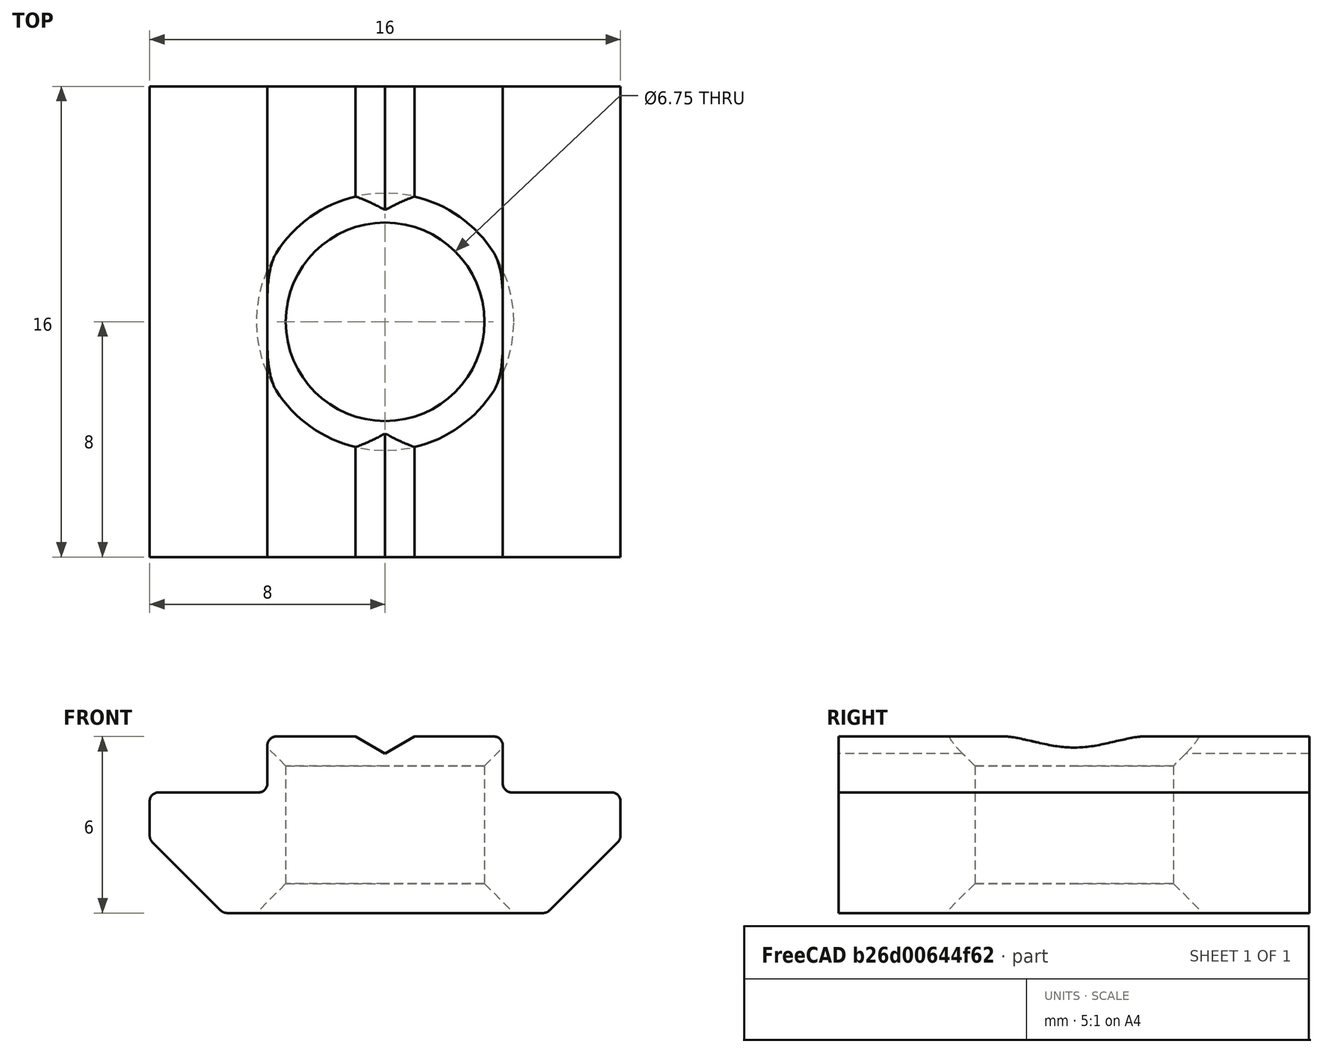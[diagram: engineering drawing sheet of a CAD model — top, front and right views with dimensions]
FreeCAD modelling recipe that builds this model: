
FCSTD DOCUMENT  (FreeCAD 0.19R20514 (Git))
Label: AP3030S8_StoneM8Heavy
Comment: FreeCAD-Library by episource -- https://github.com/episource/FreeCAD-Library
License: Creative Commons Attribution
LicenseURL: http://creativecommons.org/licenses/by/4.0/
objects: TechDraw::DrawViewDimension×10, Sketcher::SketchObject×3, TechDraw::DrawViewPart×2, TechDraw::DrawViewClip×2, TechDraw::DrawSVGTemplate×1, PartDesign::CoordinateSystem×1, App::DocumentObjectGroup×1, PartDesign::Pad×1, PartDesign::Hole×1, PartDesign::Groove×1, PartDesign::Body×1, TechDraw::DrawPage×1, App::Part×1
note: 11 computed .brp shape members not serialized (recipe doc carries the construction recipe); baked Part::Feature solids carry a one-line shape summary decoded from their .brp

FEATURE [Sketcher::SketchObject] Sketch001  label="PocketM6"
  Placement = pos=(0,0,6) rot=(0,0,1;0rad)
  sketch-geometry (1):
    g0: Circle CenterX=0 CenterY=0 CenterZ=0 NormalX=0 NormalY=0 NormalZ=1 AngleXU=0 Radius=0.715801
  constraints (1):
    c: Coincident(g0,g-1)
FEATURE [TechDraw::DrawSVGTemplate] Template
  EditableTexts = FC-SC=Scale 2:1 [mm]
  Height = 210
  Orientation = 1
  Width = 297
FEATURE [PartDesign::CoordinateSystem] AssyMount
  AttacherType = Attacher::AttachEngine3D
  AttachmentOffset = pos=(0,0,6.3) rot=(0,0,1;0rad)
  MapMode = 5
  Placement = pos=(0,0,6.3) rot=(0,0,1;0rad)
  Support = -> [XY_Plane]
  expr: .AttachmentOffset.Base.z = <<Variables>>.StoneHeight + <<Variables>>.ProfileSlotRise - <<Variables>>.StoneRise
FEATURE [App::DocumentObjectGroup] Group  label="Variables"
  ProfileSlotRise = 2.2
  ScrewHoleBevelSize = 1
  SlotWidth = 8
  StoneFillet = 0.3
  StoneHeight = 6
  StoneLength = 16
  StoneOuterRise = 1.6
  StoneTopNotchDepth = 0.58
  StoneTopNotchWidth = 2
  StoneTopRise = 1.9
  StoneWidth = 16
FEATURE [Sketcher::SketchObject] Sketch  label="StoneSectionSketch"
  MapMode = 5
  Placement = pos=(0,0,0) rot=(1,0,0;1.5708rad)
  Support = -> [XZ_Plane]
  expr: Constraints[16] = <<Variables>>.StoneFillet
  expr: Constraints[19] = <<Variables>>.StoneFillet
  expr: Constraints[23] = <<Variables>>.StoneFillet
  expr: Constraints[18] = <<Variables>>.StoneFillet
  expr: Constraints[15] = <<Variables>>.StoneFillet
  expr: Constraints[20] = <<Variables>>.StoneFillet
  expr: Constraints[24] = <<Variables>>.StoneFillet
  expr: Constraints[14] = <<Variables>>.StoneTopRise
  expr: Constraints[22] = <<Variables>>.StoneFillet
  expr: Constraints[27] = <<Variables>>.StoneTopNotchWidth
  expr: Constraints[17] = <<Variables>>.StoneFillet
  expr: Constraints[25] = <<Variables>>.StoneTopNotchDepth
  expr: Constraints[21] = <<Variables>>.StoneFillet
  expr: Constraints[13] = <<Variables>>.StoneHeight
  expr: Constraints[12] = <<Variables>>.StoneWidth
  expr: Constraints[11] = <<Variables>>.SlotWidth
  expr: Constraints[64] = <<Variables>>.StoneOuterRise
  sketch-geometry (26):
    g0: LineSegment StartX=-1 StartY=6 StartZ=0 EndX=-3.7 EndY=6 EndZ=0
    g1: ArcOfCircle CenterX=-3.7 CenterY=5.7 CenterZ=0 NormalX=0 NormalY=0 NormalZ=1 AngleXU=3.14159 Radius=0.3 StartAngle=4.71239 EndAngle=6.28319
    g2: LineSegment StartX=-4 StartY=5.7 StartZ=0 EndX=-4 EndY=4.4 EndZ=0
    g3: ArcOfCircle CenterX=-4.3 CenterY=4.4 CenterZ=0 NormalX=0 NormalY=0 NormalZ=1 AngleXU=-3.14159 Radius=0.3 StartAngle=1.5708 EndAngle=3.14159
    g4: LineSegment StartX=-4.3 StartY=4.1 StartZ=0 EndX=-7.7 EndY=4.1 EndZ=0
    g5: ArcOfCircle CenterX=-7.7 CenterY=3.8 CenterZ=0 NormalX=0 NormalY=0 NormalZ=1 AngleXU=-3.14159 Radius=0.3 StartAngle=4.71239 EndAngle=6.28319
    g6: LineSegment StartX=-8 StartY=3.8 StartZ=0 EndX=-8 EndY=2.62426 EndZ=0
    g7: ArcOfCircle CenterX=-7.7 CenterY=2.62426 CenterZ=0 NormalX=0 NormalY=0 NormalZ=1 AngleXU=-3.14159 Radius=0.3 StartAngle=0 EndAngle=0.785398
    g8: LineSegment StartX=-7.91213 StartY=2.41213 StartZ=0 EndX=-5.58787 EndY=0.087868 EndZ=0
    g9: ArcOfCircle CenterX=-5.37574 CenterY=0.3 CenterZ=0 NormalX=0 NormalY=0 NormalZ=1 AngleXU=3.14159 Radius=0.3 StartAngle=0.785398 EndAngle=1.5708
    g10: LineSegment StartX=-5.37574 StartY=0 StartZ=0 EndX=5.37574 EndY=0 EndZ=0
    g11: ArcOfCircle CenterX=5.37574 CenterY=0.3 CenterZ=0 NormalX=0 NormalY=0 NormalZ=1 AngleXU=-3.14159 Radius=0.3 StartAngle=1.5708 EndAngle=2.35619
    g12: LineSegment StartX=5.58787 StartY=0.087868 StartZ=0 EndX=7.91213 EndY=2.41213 EndZ=0
    g13: ArcOfCircle CenterX=7.7 CenterY=2.62426 CenterZ=0 NormalX=0 NormalY=0 NormalZ=1 AngleXU=-3.14159 Radius=0.3 StartAngle=2.35619 EndAngle=3.14159
    g14: LineSegment StartX=8 StartY=2.62426 StartZ=0 EndX=8 EndY=3.8 EndZ=0
    g15: ArcOfCircle CenterX=7.7 CenterY=3.8 CenterZ=0 NormalX=0 NormalY=0 NormalZ=1 AngleXU=-3.14159 Radius=0.3 StartAngle=3.14159 EndAngle=4.71239
    g16: LineSegment StartX=7.7 StartY=4.1 StartZ=0 EndX=4.3 EndY=4.1 EndZ=0
    g17: ArcOfCircle CenterX=4.3 CenterY=4.4 CenterZ=0 NormalX=0 NormalY=0 NormalZ=1 AngleXU=-3.14159 Radius=0.3 StartAngle=0 EndAngle=1.5708
    g18: LineSegment StartX=4 StartY=4.4 StartZ=0 EndX=4 EndY=5.7 EndZ=0
    g19: ArcOfCircle CenterX=3.7 CenterY=5.7 CenterZ=0 NormalX=0 NormalY=0 NormalZ=1 AngleXU=-3.14159 Radius=0.3 StartAngle=3.14159 EndAngle=4.71239
    g20: LineSegment StartX=3.7 StartY=6 StartZ=0 EndX=1 EndY=6 EndZ=0
    g21: LineSegment StartX=1 StartY=6 StartZ=0 EndX=0 EndY=5.42 EndZ=0
    g22: LineSegment StartX=0 StartY=5.42 StartZ=0 EndX=-1 EndY=6 EndZ=0
    g23: LineSegment [constr] StartX=4.3 StartY=4.1 StartZ=0 EndX=8 EndY=4.1 EndZ=0
    g24: LineSegment [constr] StartX=8 StartY=4.1 StartZ=0 EndX=8 EndY=2.5 EndZ=0
    g25: LineSegment [constr] StartX=5.58787 StartY=0.087868 StartZ=0 EndX=8 EndY=2.5 EndZ=0
  constraints (65):
    c: Horizontal(g4)
    c: Vertical(g6)
    c: Vertical(g14)
    c: Coincident(g20,g21)
    c: Coincident(g21,g22)
    c: Coincident(g22,g0)
    c: Vertical(g2)
    c: Vertical(g18)
    c: Horizontal(g10)
    c: Horizontal(g0)
    c: Horizontal(g20)
    c: DistanceX(g1,g18) = 8
    c: DistanceX(g5,g14) = 16
    c: DistanceY(g9,g0) = 6
    c: DistanceY(g16,g19) = 1.9
    c: Radius(g17) = 0.3
    c: Radius(g3) = 0.3
    c: Radius(g5) = 0.3
    c: Radius(g15) = 0.3
    c: Radius(g1) = 0.3
    c: Radius(g19) = 0.3
    c: Radius(g13) = 0.3
    c: Radius(g7) = 0.3
    c: Radius(g11) = 0.3
    c: Radius(g9) = 0.3
    c: DistanceY(g21,g20) = 0.58
    c: PointOnObject(g21,g-2)
    c: DistanceX(g0,g20) = 2
    c: Equal(g0,g20)
    c: Equal(g2,g18)
    c: Equal(g4,g16)
    c: Equal(g12,g8)
    c: Symmetric(g9,g10,g-1)
    c: Angle(g8,g6) = 2.35619
    c: Angle(g14,g12) = 2.35619
    c: Symmetric(g0,g20,g-2)
    c: Tangent(g0,g1) = -1.5708
    c: Tangent(g1,g2) = -1.5708
    c: Tangent(g19,g20) = -1.5708
    c: Tangent(g18,g19) = -1.5708
    c: Tangent(g17,g18) = 1.5708
    c: Tangent(g16,g17) = 1.5708
    c: Tangent(g15,g16) = -1.5708
    c: Tangent(g14,g15) = -1.5708
    c: Tangent(g13,g14) = -1.5708
    c: Tangent(g12,g13) = -1.5708
    c: Tangent(g11,g12) = -1.5708
    c: Tangent(g10,g11) = -1.5708
    c: Tangent(g9,g10) = -1.5708
    c: Tangent(g8,g9) = -1.5708
    c: Tangent(g7,g8) = -1.5708
    c: Tangent(g6,g7) = -1.5708
    c: Tangent(g5,g6) = -1.5708
    c: Tangent(g4,g5) = -1.5708
    c: Tangent(g3,g4) = 1.5708
    c: Tangent(g2,g3) = 1.5708
    c: Coincident(g23,g16)
    c: PointOnObject(g15,g23)
    c: PointOnObject(g13,g24)
    c: PointOnObject(g14,g24)
    c: PointOnObject(g12,g25)
    c: Coincident(g24,g23)
    c: Coincident(g25,g11)
    c: Coincident(g24,g25)
    c: DistanceY(g24,g23) = 1.6
FEATURE [PartDesign::Pad] Pad
  AllowMultiFace = false
  Length = 16
  Length2 = 100
  Midplane = true
  Placement = pos=(0,0,0) rot=(1,0,0;1.5708rad)
  Profile = -> Sketch
  Type = 0
FEATURE [PartDesign::Hole] Hole
  AllowMultiFace = false
  BaseFeature = -> Pad
  Depth = 25
  DepthType = 1
  Diameter = 6.75
  DrillPoint = 1
  DrillPointAngle = 118
  HoleCutCountersinkAngle = 90
  HoleCutDepth = 0
  HoleCutDiameter = 8
  HoleCutType = 0
  ModelActualThread = false
  Placement = pos=(0,0,0) rot=(1,0,0;1.5708rad)
  Profile = -> Sketch001
  Tapered = false
  TaperedAngle = 90
  ThreadAngle = 60
  ThreadClass = 0
  ThreadCutOffInner = 0.135316
  ThreadCutOffOuter = 0.270633
  ThreadDirection = 1
  ThreadFit = 0
  ThreadPitch = 1.25
  ThreadSize = 8
  ThreadType = 1
  Threaded = true
FEATURE [Sketcher::SketchObject] Sketch002  label="SketchScrewHoleBevel"
  ExternalGeometry = -> [Hole]
  MapMode = 5
  Placement = pos=(0,0,0) rot=(0.57735,0.57735,0.57735;2.0944rad)
  Support = -> [YZ_Plane]
  expr: Constraints[6] = <<Variables>>.StoneHeight
  expr: Constraints[5] = <<Variables>>.ScrewHoleBevelSize
  sketch-geometry (8):
    g0: LineSegment [constr] StartX=3.375 StartY=0 StartZ=0 EndX=3.375 EndY=6 EndZ=0
    g1: LineSegment [constr] StartX=4.375 StartY=0 StartZ=0 EndX=4.375 EndY=6 EndZ=0
    g2: LineSegment StartX=3.375 StartY=6 StartZ=0 EndX=4.375 EndY=6 EndZ=0
    g3: LineSegment StartX=4.375 StartY=6 StartZ=0 EndX=3.375 EndY=5 EndZ=0
    g4: LineSegment StartX=3.375 StartY=5 StartZ=0 EndX=3.375 EndY=6 EndZ=0
    g5: LineSegment StartX=3.375 StartY=0 StartZ=0 EndX=3.375 EndY=1 EndZ=0
    g6: LineSegment StartX=3.375 StartY=1 StartZ=0 EndX=4.375 EndY=0 EndZ=0
    g7: LineSegment StartX=4.375 StartY=0 StartZ=0 EndX=3.375 EndY=0 EndZ=0
  constraints (22):
    c: PointOnObject(g0,g-1)
    c: Vertical(g0)
    c: PointOnObject(g-3,g0)
    c: Vertical(g1)
    c: PointOnObject(g1,g-1)
    c: DistanceX(g0,g1) = 1
    c: DistanceY(g0,g0) = 6
    c: Equal(g0,g1)
    c: Coincident(g0,g2)
    c: Coincident(g2,g1)
    c: Coincident(g2,g3)
    c: PointOnObject(g3,g0)
    c: Coincident(g3,g4)
    c: Coincident(g4,g2)
    c: Equal(g4,g2)
    c: Coincident(g0,g5)
    c: PointOnObject(g5,g0)
    c: Coincident(g5,g6)
    c: Coincident(g6,g1)
    c: Coincident(g6,g7)
    c: Coincident(g7,g5)
    c: Equal(g5,g7)
FEATURE [PartDesign::Groove] Groove  label="ScrewHoleBevel"
  Angle = 360
  Axis = (-2e-16,3e-16,1)
  Base = (0,0,0)
  BaseFeature = -> Hole
  Placement = pos=(0,0,0) rot=(1,0,0;1.5708rad)
  Profile = -> Sketch002
  ReferenceAxis = -> Sketch002 [V_Axis]
FEATURE [PartDesign::Body] Body
  Group = -> [Pad,Sketch001,Hole,Sketch,Sketch002,Groove]
  Origin = -> Origin
  Tip = -> Groove
FEATURE [TechDraw::DrawViewPart] View
  CoarseView = false
  Direction = (0,0,1)
  Focus = 100
  HardHidden = false
  IsoCount = 0
  IsoHidden = false
  IsoVisible = false
  LockPosition = false
  Perspective = false
  Rotation = 0
  Scale = 2
  ScaleType = 0
  SeamHidden = false
  SeamVisible = false
  SmoothHidden = false
  SmoothVisible = false
  Source = -> [Body]
  X = 0
  XDirection = (1,0,0)
  Y = -3
FEATURE [TechDraw::DrawViewClip] Clip  label="Top View"
  Height = 60
  LockPosition = false
  Rotation = 0
  Scale = 2
  ScaleType = 0
  ShowFrame = false
  Views = -> [View]
  Width = 100
  X = 75
  Y = 110
FEATURE [TechDraw::DrawViewDimension] Dimension003
  Arbitrary = false
  FormatSpec = %.1f
  Inverted = false
  LockPosition = false
  MeasureType = 1
  OverTolerance = 0
  References2D = -> [View]
  Rotation = 0
  Scale = 2
  ScaleType = 0
  TheoreticalExact = false
  Type = 2
  UnderTolerance = 0
  X = -26.0269
  Y = 0.752239
FEATURE [TechDraw::DrawViewPart] View001
  CoarseView = false
  Direction = (0,-1,0)
  Focus = 100
  HardHidden = false
  IsoCount = 0
  IsoHidden = false
  IsoVisible = false
  LockPosition = false
  Perspective = false
  Rotation = 0
  Scale = 2
  ScaleType = 0
  SeamHidden = false
  SeamVisible = false
  SmoothHidden = false
  SmoothVisible = false
  Source = -> [Body]
  X = 0
  XDirection = (1,0,0)
  Y = 0
FEATURE [TechDraw::DrawViewClip] Clip001  label="Front View"
  Height = 50
  LockPosition = false
  Rotation = 0
  Scale = 2
  ScaleType = 0
  ShowFrame = false
  Views = -> [View001]
  Width = 100
  X = 222
  Y = 110
FEATURE [TechDraw::DrawViewDimension] Dimension004
  Arbitrary = false
  FormatSpec = %.1f
  Inverted = false
  LockPosition = false
  MeasureType = 1
  OverTolerance = 0
  References2D = -> [View001]
  Rotation = 0
  Scale = 2
  ScaleType = 0
  TheoreticalExact = false
  Type = 2
  UnderTolerance = 0
  X = -30.0026
  Y = -1.62532
FEATURE [TechDraw::DrawViewDimension] Dimension005
  Arbitrary = false
  FormatSpec = %.1f
  Inverted = false
  LockPosition = false
  MeasureType = 1
  OverTolerance = 0
  References2D = -> [View001]
  Rotation = 0
  Scale = 2
  ScaleType = 0
  TheoreticalExact = false
  Type = 2
  UnderTolerance = 0
  X = 21.6395
  Y = 0.824036
FEATURE [TechDraw::DrawViewDimension] Dimension006
  Arbitrary = false
  FormatSpec = %.1f
  Inverted = false
  LockPosition = false
  MeasureType = 1
  OverTolerance = 0
  References2D = -> [View001]
  Rotation = 0
  Scale = 2
  ScaleType = 0
  TheoreticalExact = false
  Type = 1
  UnderTolerance = 0
  X = -0.572247
  Y = -10.8941
FEATURE [TechDraw::DrawViewDimension] Dimension007
  Arbitrary = false
  FormatSpec = %.1f
  Inverted = false
  LockPosition = false
  MeasureType = 1
  OverTolerance = 0
  References2D = -> [View001]
  Rotation = 0
  Scale = 2
  ScaleType = 0
  TheoreticalExact = false
  Type = 1
  UnderTolerance = 0
  X = 13.3352
  Y = 13.4542
FEATURE [TechDraw::DrawViewDimension] Dimension008
  Arbitrary = false
  FormatSpec = %.1f
  Inverted = false
  LockPosition = false
  MeasureType = 1
  OverTolerance = 0
  References2D = -> [View001]
  Rotation = 0
  Scale = 2
  ScaleType = 0
  TheoreticalExact = false
  Type = 1
  UnderTolerance = 0
  X = 0.476873
  Y = 20.1582
FEATURE [TechDraw::DrawViewDimension] Dimension009
  Arbitrary = false
  FormatSpec = %.1f
  Inverted = false
  LockPosition = false
  MeasureType = 1
  OverTolerance = 0
  References2D = -> [View001]
  Rotation = 0
  Scale = 2
  ScaleType = 0
  TheoreticalExact = false
  Type = 2
  UnderTolerance = 0
  X = -21.6866
  Y = 7.86119
FEATURE [TechDraw::DrawViewDimension] Dimension
  Arbitrary = false
  FormatSpec = %.1f
  Inverted = false
  LockPosition = false
  MeasureType = 1
  OverTolerance = 0
  References2D = -> [View]
  Rotation = 0
  Scale = 2
  ScaleType = 0
  TheoreticalExact = false
  Type = 1
  UnderTolerance = 0
  X = 0.276739
  Y = 22.4196
FEATURE [TechDraw::DrawViewDimension] Dimension010
  Arbitrary = false
  FormatSpec = %.1f
  Inverted = false
  LockPosition = false
  MeasureType = 1
  OverTolerance = 0
  References2D = -> [View]
  Rotation = 0
  Scale = 2
  ScaleType = 0
  TheoreticalExact = false
  Type = 1
  UnderTolerance = 0
  X = 12.1468
  Y = 29.2987
FEATURE [TechDraw::DrawViewDimension] Dimension011
  Arbitrary = false
  FormatSpec = %.1f
  Inverted = false
  LockPosition = false
  MeasureType = 1
  OverTolerance = 0
  References2D = -> [View]
  Rotation = 0
  Scale = 2
  ScaleType = 0
  TheoreticalExact = false
  Type = 1
  UnderTolerance = 0
  X = -11.8138
  Y = 29.3106
FEATURE [TechDraw::DrawPage] Page  label="Spec"
  KeepUpdated = true
  NextBalloonIndex = 1
  ProjectionType = 0
  Scale = 2
  Template = -> Template
  Views = -> [View,Clip,Dimension003,Clip001,View001,Dimension004,Dimension005,Dimension006,Dimension007,Dimension008,Dimension009,Dimension,Dimension010,Dimension011]
FEATURE [App::Part] Part  label="AP3030S8_StoneM8Heavy"
  Group = -> [Body,Page,AssyMount,Group]
  Origin = -> Origin001
